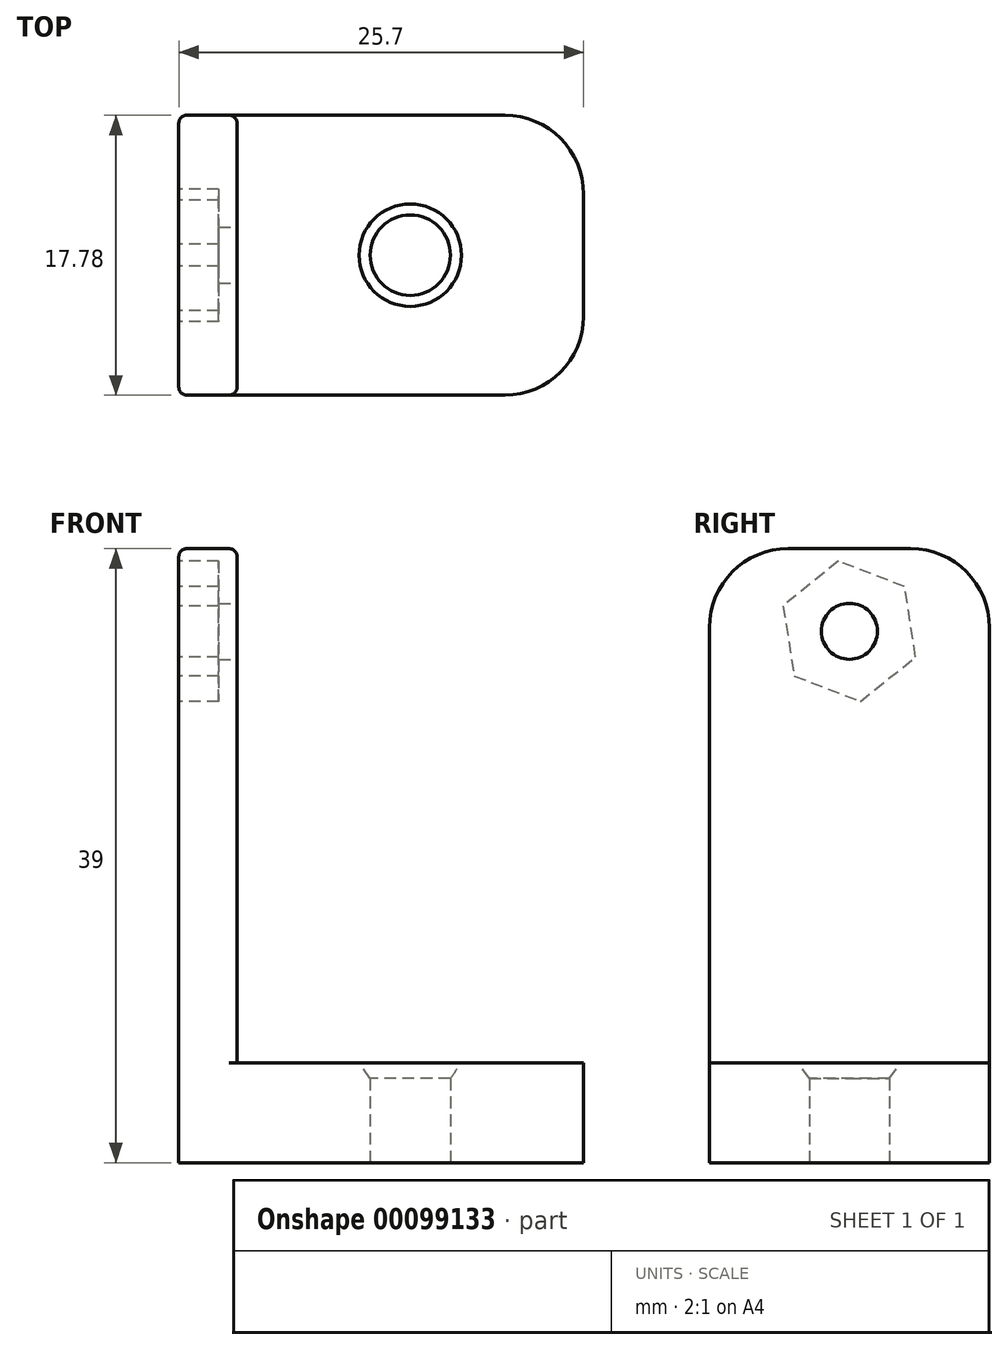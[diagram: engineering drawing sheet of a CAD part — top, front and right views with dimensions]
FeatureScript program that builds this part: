
annotation { "Feature Type Name" : "Feature", "Feature Type Description" : "" }
export const myFeature = defineFeature(function(context is Context, id is Id, definition is map)
    precondition{}
    {
        {
            var Q0;
            Q0=qCreatedBy(makeId("Top.planeOp"),FACE);
            var sketch = newSketch(context, id + "F0", { "sketchPlane" : qUnion([Q0])});
            skLineSegment(sketch, "E0.bottom", {"start": v(11, 8.9) * mm, "end": v(-11, 8.9) * mm});
            skLineSegment(sketch, "E0.top", {"start": v(11, -8.89) * mm, "end": v(-11, -8.89) * mm});
            skLineSegment(sketch, "E0.left", {"start": v(11, 8.9) * mm, "end": v(11, -8.89) * mm});
            skLineSegment(sketch, "E0.right", {"start": v(-11, 8.9) * mm, "end": v(-11, -8.89) * mm});
            skPoint(sketch, "E0.middle", {"position": v(0, 0) * mm});
            skSolve(sketch);
        }
        {
            var Q0;
            Q0 = qSketchRegion(id + "F0", true);
            extrude(context, id + "F1", {"entities" : qUnion([Q0]), "depth" : 6.35 * mm});
        }
        {
            var Q0;
            Q0=qCreatedBy(makeId("Top.planeOp"),FACE);
            var sketch = newSketch(context, id + "F2", { "sketchPlane" : qUnion([Q0])});
            skLineSegment(sketch, "E1", {"start": v(-14.7, 8.9) * mm, "end": v(-14.7, -8.9) * mm});
            skLineSegment(sketch, "E2", {"start": v(-14.7, -8.9) * mm, "end": v(-11, -8.9) * mm});
            skLineSegment(sketch, "E3.MirrorCS", {"start": v(-14.7, 8.9) * mm, "end": v(-11, 8.9) * mm});
            skPoint(sketch, "E4.orphan", {"position": v(-14.5, 8.9) * mm});
            skPoint(sketch, "E5.orphan", {"position": v(-14.5, -8.9) * mm});
            skLineSegment(sketch, "E6", {"start": v(-11, -8.9) * mm, "end": v(-11, 8.9) * mm});
            skPoint(sketch, "E7.orphan", {"position": v(11.17, 8.89) * mm});
            skPoint(sketch, "E8.orphan", {"position": v(11.17, -8.89) * mm});
            skSolve(sketch);
        }
        {
            var Q0;
            Q0=makeQuery(id+"F2.imprint","IMPRINT",FACE,{"disambiguationData":[TD([[makeQuery(id+"F2.imprint","IMPRINT",EDGE,{"derivedFrom":sQuery(id+"F2.wireOp",EDGE,"E1")}),1.0]])]});
            extrude(context, id + "F3", {"entities" : qUnion([Q0]), "operationType" : NewBodyOperationType.ADD, "depth" : 39 * mm});
        }
        {
            var Q0;
            Q0=makeQuery(id+"F1.opExtrude","CAP_FACE",FACE,{"disambiguationData":[OSD([sQuery(id+"F0.wireOp",EDGE,"E0.bottom"),sQuery(id+"F0.wireOp",EDGE,"E0.top"),sQuery(id+"F0.wireOp",EDGE,"E0.left"),sQuery(id+"F0.wireOp",EDGE,"E0.right")])],"isStart":false});
            var sketch = newSketch(context, id + "F4", { "sketchPlane" : qUnion([Q0])});
            skCircle(sketch, "E9", {"center": v(0, 0) * mm, "radius": 3.25 * mm});
            skSolve(sketch);
        }
        {
            var Q0;
            Q0=makeQuery(id+"F4.imprint","IMPRINT",FACE,{"disambiguationData":[TD([[makeQuery(id+"F4.imprint","IMPRINT",EDGE,{"derivedFrom":sQuery(id+"F4.wireOp",EDGE,"E9")}),-1.0]])]});
            cPlane(context, id + "F5", {"entities" : qUnion([Q0]), "cplaneType" : CPlaneType.OFFSET, "offset" : 2.46 * mm, "oppositeDirection" : true, "width" : 150 * mm, "height" : 150 * mm});
        }
        {
            var Q0;
            Q0=qCreatedBy(makeId("Top.planeOp"),FACE);
            var sketch = newSketch(context, id + "F6", { "sketchPlane" : qUnion([Q0])});
            skCircle(sketch, "E10", {"center": v(0, 0) * mm, "radius": 2.55 * mm});
            skSolve(sketch);
        }
        {
            var Q0;
            Q0=qCreatedBy(id+"F5.planeOp",FACE);
            var sketch = newSketch(context, id + "F7", { "sketchPlane" : qUnion([Q0])});
            skCircle(sketch, "E11", {"center": v(0, 0) * mm, "radius": 1.52 * mm});
            skSolve(sketch);
        }
        {
            var Q0;
            Q0=makeQuery(id+"F6.imprint","IMPRINT",FACE,{"disambiguationData":[TD([[makeQuery(id+"F6.imprint","IMPRINT",EDGE,{"derivedFrom":sQuery(id+"F6.wireOp",EDGE,"E10")}),1.0]])]});
            extrude(context, id + "F8", {"entities" : qUnion([Q0]), "operationType" : NewBodyOperationType.REMOVE, "depth" : 25 * mm});
        }
        {
            var Q1;
            Q1=makeQuery(id+"F4.imprint","IMPRINT",FACE,{"disambiguationData":[TD([[makeQuery(id+"F4.imprint","IMPRINT",EDGE,{"derivedFrom":sQuery(id+"F4.wireOp",EDGE,"E9")}),1.0]])]});
            var Q2;
            Q2=makeQuery(id+"F7.imprint","IMPRINT",FACE,{"disambiguationData":[TD([[makeQuery(id+"F7.imprint","IMPRINT",EDGE,{"derivedFrom":sQuery(id+"F7.wireOp",EDGE,"E11")}),1.0]])]});
            loft(context, id + "F9", {"operationType" : NewBodyOperationType.REMOVE, "sheetProfilesArray" : [{ "sheetProfileEntities" : qUnion([Q1]) }, { "sheetProfileEntities" : qUnion([Q2]) }]});
        }
        {
            var Q0;
            Q0=makeQuery(id+"F3.opExtrude","SWEPT_FACE",FACE,{"disambiguationData":[OSD([sQuery(id+"F2.wireOp",EDGE,"E6")])]});
            var sketch = newSketch(context, id + "F10", { "sketchPlane" : qUnion([Q0])});
            skLineSegment(sketch, "E12", {"start": v(19.41, 33.75) * mm, "end": v(-23.1, 33.75) * mm, "construction": true});
            skCircle(sketch, "E13", {"center": v(0, 33.75) * mm, "radius": 1.78 * mm});
            skLineSegment(sketch, "E14.0.0", {"start": v(8.89, 0) * mm, "end": v(-8.9, 0) * mm});
            skLineSegment(sketch, "E14.0.1", {"start": v(-8.9, 0) * mm, "end": v(-8.9, 39) * mm});
            skLineSegment(sketch, "E14.0.2", {"start": v(-8.9, 39) * mm, "end": v(8.9, 39) * mm});
            skLineSegment(sketch, "E14.0.3", {"start": v(8.9, 39) * mm, "end": v(8.9, 0) * mm});
            skSolve(sketch);
        }
        {
            var Q0;
            Q0=makeQuery(id+"F10.imprint","IMPRINT",FACE,{"disambiguationData":[TD([[makeQuery(id+"F10.imprint","IMPRINT",EDGE,{"derivedFrom":sQuery(id+"F10.wireOp",EDGE,"E13")}),1.0]])]});
            extrude(context, id + "F11", {"entities" : qUnion([Q0]), "operationType" : NewBodyOperationType.REMOVE, "oppositeDirection" : true, "depth" : 25 * mm});
        }
        {
            var Q0;
            Q0=makeQuery(id+"F3.opExtrude","SWEPT_FACE",FACE,{"disambiguationData":[OSD([sQuery(id+"F2.wireOp",EDGE,"E1")])]});
            var sketch = newSketch(context, id + "F12", { "sketchPlane" : qUnion([Q0])});
            skCircle(sketch, "E15.cCircle", {"center": v(0, 33.75) * mm, "radius": 4.5 * mm, "construction": true});
            skLineSegment(sketch, "E15.0", {"start": v(4.2, 35.37) * mm, "end": v(3.5, 30.92) * mm});
            skLineSegment(sketch, "E15.1", {"start": v(3.5, 30.92) * mm, "end": v(-0.7, 29.3) * mm});
            skLineSegment(sketch, "E15.2", {"start": v(-0.7, 29.3) * mm, "end": v(-4.2, 32.13) * mm});
            skLineSegment(sketch, "E15.3", {"start": v(-4.2, 32.13) * mm, "end": v(-3.5, 36.58) * mm});
            skLineSegment(sketch, "E15.4", {"start": v(-3.5, 36.58) * mm, "end": v(0.7, 38.2) * mm});
            skLineSegment(sketch, "E15.5", {"start": v(0.7, 38.2) * mm, "end": v(4.2, 35.37) * mm});
            skSolve(sketch);
        }
        {
            var Q0;
            Q0=makeQuery(id+"F12.imprint","IMPRINT",FACE,{"disambiguationData":[TD([[makeQuery(id+"F12.imprint","IMPRINT",EDGE,{"derivedFrom":sQuery(id+"F12.wireOp",EDGE,"E15.0")}),-1.0]])]});
            extrude(context, id + "F13", {"entities" : qUnion([Q0]), "operationType" : NewBodyOperationType.REMOVE, "oppositeDirection" : true, "depth" : 2.54 * mm});
        }
        {
            var Q0;
            Q0=makeQuery(id+"F1.opExtrude","SWEPT_EDGE",EDGE,{"disambiguationData":[OSD([sQuery(id+"F0.wireOp",EDGE,"E0.bottom"),sQuery(id+"F0.wireOp",EDGE,"E0.left")])]});
            var Q1;
            Q1=makeQuery(id+"F1.opExtrude","SWEPT_EDGE",EDGE,{"disambiguationData":[OSD([sQuery(id+"F0.wireOp",EDGE,"E0.top"),sQuery(id+"F0.wireOp",EDGE,"E0.left")])]});
            var Q2;
            Q2=makeQuery(id+"F3.opExtrude","CAP_EDGE",EDGE,{"disambiguationData":[OSD([sQuery(id+"F2.wireOp",EDGE,"E3.MirrorCS")])],"isStart":false});
            var Q3;
            Q3=makeQuery(id+"F3.opExtrude","CAP_EDGE",EDGE,{"disambiguationData":[OSD([sQuery(id+"F2.wireOp",EDGE,"E2")])],"isStart":false});
            fillet(context, id + "F14", {"entities" : qUnion([Q0, Q1, Q2, Q3]), "radius" : 5 * mm, "tangentPropagation" : true, "allowEdgeOverflow" : false});
        }
        {
            var Q0;
            Q0=makeQuery(id+"F3.opExtrude","SWEPT_EDGE",EDGE,{"disambiguationData":[OSD([sQuery(id+"F2.wireOp",EDGE,"E2"),sQuery(id+"F2.wireOp",EDGE,"E6")])]});
            var Q1;
            Q1=makeQuery(id+"F1.opExtrude","CAP_EDGE",EDGE,{"disambiguationData":[OSD([sQuery(id+"F0.wireOp",EDGE,"E0.right")])],"isStart":false});
            var Q2;
            Q2=makeQuery(id+"F3.opExtrude","SWEPT_EDGE",EDGE,{"disambiguationData":[OSD([sQuery(id+"F2.wireOp",EDGE,"E1"),sQuery(id+"F2.wireOp",EDGE,"E2")])]});
            var Q3;
            Q3=makeQuery(id+"F14.opFillet","BLEND_EDGE",EDGE,{"blendedFrom":[makeQuery(id+"F3.opExtrude","CAP_EDGE",EDGE,{"disambiguationData":[OSD([sQuery(id+"F2.wireOp",EDGE,"E2")])],"isStart":false}),makeQuery(id+"F3.opExtrude","SWEPT_FACE",FACE,{"disambiguationData":[OSD([sQuery(id+"F2.wireOp",EDGE,"E1")])]})],"blendedInto":[makeQuery(id+"F3.opExtrude","SWEPT_FACE",FACE,{"disambiguationData":[OSD([sQuery(id+"F2.wireOp",EDGE,"E1")])]})]});
            fillet(context, id + "F15", {"entities" : qUnion([Q0, Q1, Q2, Q3]), "radius" : .5 * mm, "tangentPropagation" : true, "allowEdgeOverflow" : false});
        }
    });
